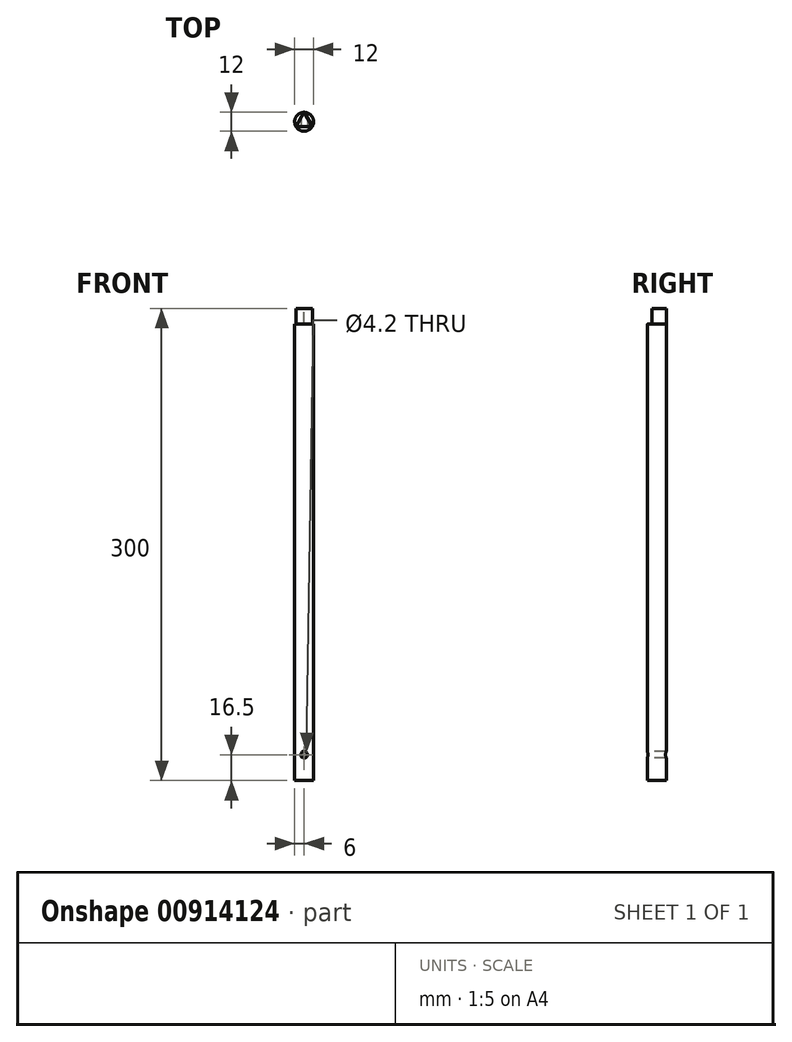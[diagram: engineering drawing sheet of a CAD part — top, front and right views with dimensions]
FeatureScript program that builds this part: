
annotation { "Feature Type Name" : "Feature", "Feature Type Description" : "" }
export const myFeature = defineFeature(function(context is Context, id is Id, definition is map)
    precondition{}
    {
        {
            var Q0;
            Q0=qCreatedBy(makeId("Top.planeOp"),FACE);
            var sketch = newSketch(context, id + "F0", { "sketchPlane" : qUnion([Q0])});
            skCircle(sketch, "E0", {"center": v(0, 0) * mm, "radius": 6 * mm});
            skSolve(sketch);
        }
        {
            var Q0;
            Q0 = qSketchRegion(id + "F0", true);
            extrude(context, id + "F1", {"entities" : qUnion([Q0]), "depth" : 300 * mm, "offsetDistance" : 25 * mm});
        }
        {
            var Q0;
            Q0=makeQuery(id+"F1.opExtrude","CAP_FACE",FACE,{"disambiguationData":[OSD([sQuery(id+"F0.wireOp",EDGE,"E0")])],"isStart":false});
            var sketch = newSketch(context, id + "F2", { "sketchPlane" : qUnion([Q0])});
            skLineSegment(sketch, "E1", {"start": v(-5.2, -3) * mm, "end": v(5.2, -3) * mm});
            skLineSegment(sketch, "E2", {"start": v(5.2, -3) * mm, "end": v(0, 6) * mm});
            skLineSegment(sketch, "E3", {"start": v(0, 6) * mm, "end": v(-5.2, -3) * mm});
            skLineSegment(sketch, "E4", {"start": v(5.2, -3) * mm, "end": v(-2.6, 1.5) * mm, "construction": true});
            skCircle(sketch, "E5.0", {"center": v(0, 0) * mm, "radius": 11 * mm});
            skSolve(sketch);
        }
        {
            var Q0;
            Q0 = qSketchRegion(id + "F2", true);
            extrude(context, id + "F3", {"entities" : qUnion([Q0]), "operationType" : NewBodyOperationType.REMOVE, "oppositeDirection" : true, "depth" : 10 * mm, "offsetDistance" : 25 * mm});
        }
        {
            var Q0;
            Q0=makeQuery(id+"F3.boolean.opBoolean","COPY",EDGE,{"derivedFrom":makeQuery(id+"F3.opExtrude","CAP_EDGE",EDGE,{"disambiguationData":[OSD([sQuery(id+"F2.wireOp",EDGE,"E1")])],"isStart":false})});
            fillet(context, id + "F4", {"entities" : qUnion([Q0]), "radius" : 0.2 * mm, "tangentPropagation" : true, "allowEdgeOverflow" : false});
        }
        {
            var Q0;
            Q0=makeQuery(id+"F3.boolean.opBoolean","COPY",EDGE,{"derivedFrom":makeQuery(id+"F3.opExtrude","CAP_EDGE",EDGE,{"disambiguationData":[OSD([sQuery(id+"F2.wireOp",EDGE,"E3")])],"isStart":false})});
            fillet(context, id + "F5", {"entities" : qUnion([Q0]), "radius" : 0.2 * mm, "tangentPropagation" : true, "allowEdgeOverflow" : false});
        }
        {
            var Q0;
            Q0=makeQuery(id+"F3.boolean.opBoolean","COPY",EDGE,{"derivedFrom":makeQuery(id+"F3.opExtrude","CAP_EDGE",EDGE,{"disambiguationData":[OSD([sQuery(id+"F2.wireOp",EDGE,"E2")])],"isStart":false})});
            fillet(context, id + "F6", {"entities" : qUnion([Q0]), "radius" : 0.2 * mm, "tangentPropagation" : true, "allowEdgeOverflow" : false});
        }
        {
            var Q0;
            Q0=qCreatedBy(makeId("Front.planeOp"),FACE);
            cPlane(context, id + "F7", {"entities" : qUnion([Q0]), "cplaneType" : CPlaneType.OFFSET, "offset" : 6 * mm, "width" : 150 * mm, "height" : 150 * mm});
        }
        {
            var Q0;
            Q0=qCreatedBy(id+"F7.planeOp",FACE);
            var sketch = newSketch(context, id + "F8", { "sketchPlane" : qUnion([Q0])});
            skPoint(sketch, "E6", {"position": v(0, 16.5) * mm});
            skSolve(sketch);
        }
        {
            var Q0;
            Q0=sQuery(id+"F8.wireOp",VERTEX,"E6");
            var Q1;
            Q1=makeQuery(id+"F1.opExtrude","SWEPT_BODY",BODY,{"disambiguationData":[OSD([sQuery(id+"F0.wireOp",EDGE,"E0")])]});
            hole(context, id + "F9", {"style" : HoleStyle.SIMPLE, "endStyle" : HoleEndStyle.THROUGH, "standardTappedOrClearance" : lookupTablePath({ "standard" : "ISO", "engagement" : "75%", "pitch" : "0.8 mm", "size" : "M5", "type" : "Tapped" }), "standardBlindInLast" : lookupTablePath({ "standard" : "ISO", "fit" : "Normal", "engagement" : "75%", "pitch" : "0.8 mm", "size" : "M5", "type" : "Clearance & tapped" }), "holeDiameter" : 4.2 * mm, "majorDiameter" : 5 * mm, "showTappedDepth" : true, "isTappedThrough" : true, "tappedDepth" : 14 * mm, "tapClearance" : 3, "locations" : qUnion([Q0]), "scope" : qUnion([Q1])});
        }
    });
